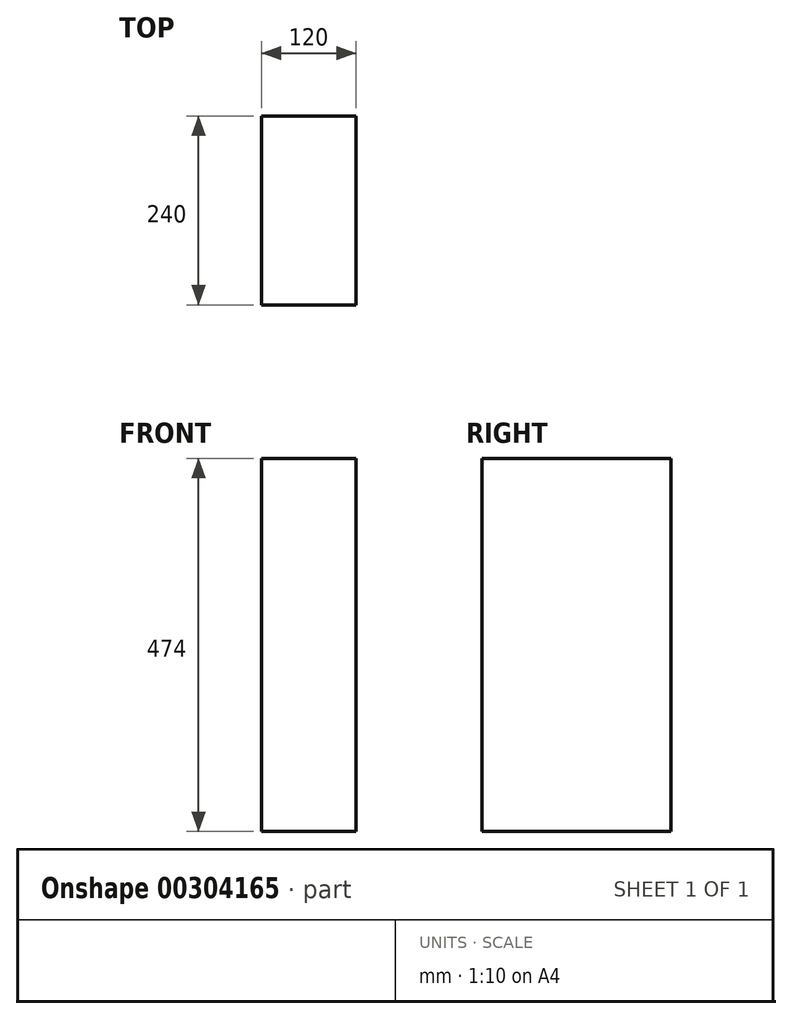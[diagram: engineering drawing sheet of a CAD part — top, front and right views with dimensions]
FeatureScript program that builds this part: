
annotation { "Feature Type Name" : "Feature", "Feature Type Description" : "" }
export const myFeature = defineFeature(function(context is Context, id is Id, definition is map)
    precondition{}
    {
        {
            var Q0;
            Q0=qCreatedBy(makeId("Top.planeOp"),FACE);
            var sketch = newSketch(context, id + "F0", { "sketchPlane" : qUnion([Q0])});
            skLineSegment(sketch, "E0.bottom", {"start": v(-54.34, 152.88) * mm, "end": v(65.66, 152.88) * mm});
            skLineSegment(sketch, "E0.top", {"start": v(-54.34, -87.12) * mm, "end": v(65.66, -87.12) * mm});
            skLineSegment(sketch, "E0.left", {"start": v(-54.34, 152.88) * mm, "end": v(-54.34, -87.12) * mm});
            skLineSegment(sketch, "E0.right", {"start": v(65.66, 152.88) * mm, "end": v(65.66, -87.12) * mm});
            skSolve(sketch);
        }
        {
            var Q0;
            Q0=makeQuery(id+"F0.imprint","IMPRINT",FACE,{"disambiguationData":[TD([[makeQuery(id+"F0.imprint","IMPRINT",EDGE,{"derivedFrom":sQuery(id+"F0.wireOp",EDGE,"E0.bottom")}),-1.0]])]});
            extrude(context, id + "F1", {"entities" : qUnion([Q0]), "depth" : 474 * mm});
        }
    });
